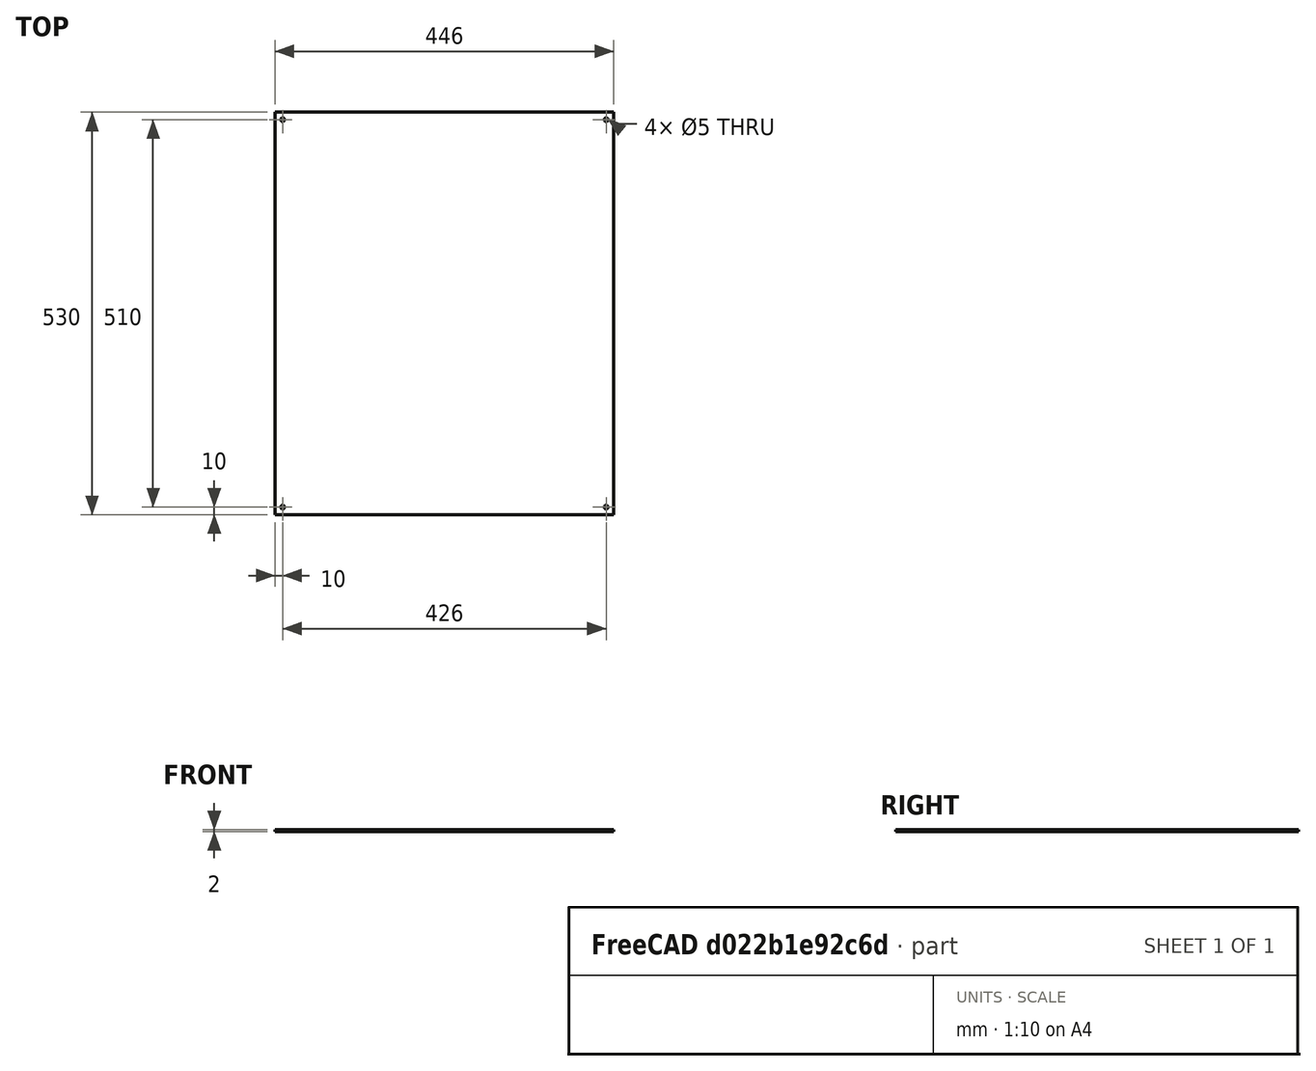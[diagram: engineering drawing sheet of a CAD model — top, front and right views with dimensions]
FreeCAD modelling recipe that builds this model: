
FCSTD DOCUMENT  (FreeCAD 0.16R6698 (Git))
Label: Plaque laté switch
License: All rights reserved
LicenseURL: http://en.wikipedia.org/wiki/All_rights_reserved
objects: Sketcher::SketchObject×1, PartDesign::Pad×1
note: 3 computed .brp shape members not serialized (recipe doc carries the construction recipe); baked Part::Feature solids carry a one-line shape summary decoded from their .brp

FEATURE [Sketcher::SketchObject] Sketch
  sketch-geometry (8):
    g0: LineSegment StartX=-223 StartY=265 StartZ=0 EndX=223 EndY=265 EndZ=0
    g1: LineSegment StartX=223 StartY=265 StartZ=0 EndX=223 EndY=-265 EndZ=0
    g2: LineSegment StartX=223 StartY=-265 StartZ=0 EndX=-223 EndY=-265 EndZ=0
    g3: LineSegment StartX=-223 StartY=-265 StartZ=0 EndX=-223 EndY=265 EndZ=0
    g4: Circle CenterX=-213 CenterY=255 CenterZ=0 NormalX=0 NormalY=0 NormalZ=1 Radius=2.5
    g5: Circle CenterX=-213 CenterY=-255 CenterZ=0 NormalX=0 NormalY=0 NormalZ=1 Radius=2.5
    g6: Circle CenterX=213 CenterY=-255 CenterZ=0 NormalX=0 NormalY=0 NormalZ=1 Radius=2.5
    g7: Circle CenterX=213 CenterY=255 CenterZ=0 NormalX=0 NormalY=0 NormalZ=1 Radius=2.5
  constraints (24):
    c: Coincident(g0,g1)
    c: Coincident(g1,g2)
    c: Coincident(g2,g3)
    c: Coincident(g3,g0)
    c: Horizontal(g0)
    c: Horizontal(g2)
    c: Vertical(g1)
    c: Vertical(g3)
    c: DistanceX(g0,g0) = 446
    c: DistanceY(g1,g1) = 530
    c: DistanceX(g-1,g0) = 223
    c: DistanceY(g-1,g0) = 265
    c: Radius(g7) = 2.5
    c: Equal(g7,g4)
    c: Equal(g7,g5)
    c: Equal(g7,g6)
    c: DistanceY(g4,g0) = 10
    c: DistanceX(g0,g4) = 10
    c: DistanceX(g7,g0) = 10
    c: DistanceY(g7,g0) = 10
    c: DistanceX(g6,g1) = 10
    c: DistanceY(g1,g6) = 10
    c: DistanceX(g2,g5) = 10
    c: DistanceY(g2,g5) = 10
FEATURE [PartDesign::Pad] Pad
  Length = 2
  Length2 = 100
  Sketch = -> Sketch
  Type = 0
